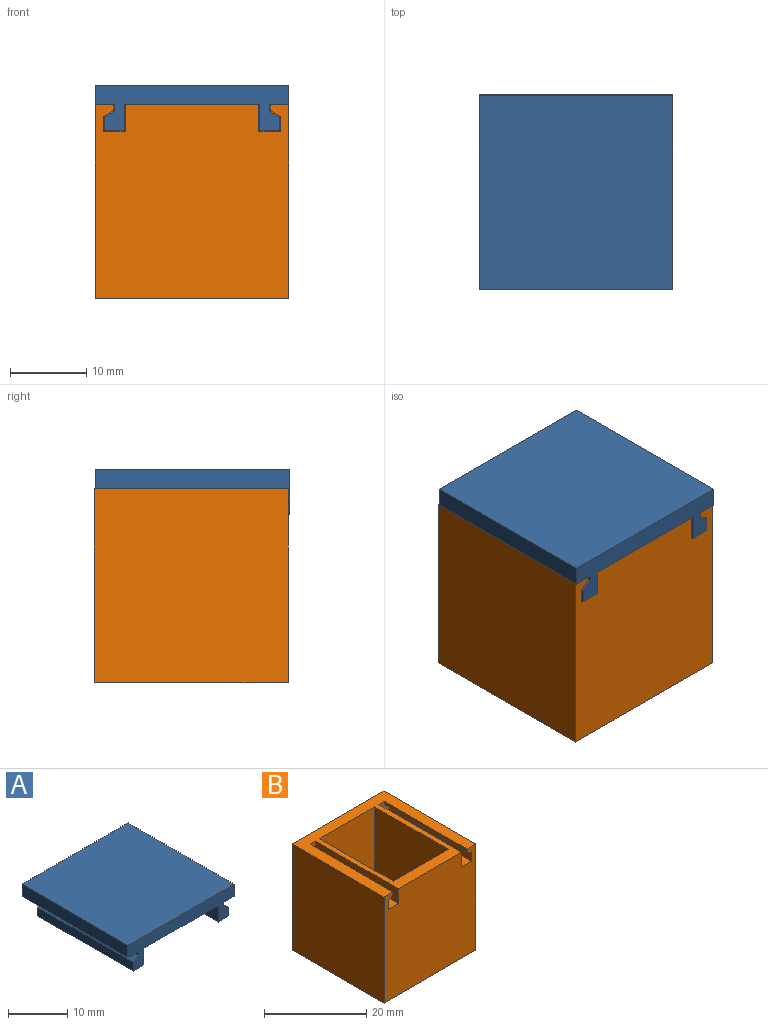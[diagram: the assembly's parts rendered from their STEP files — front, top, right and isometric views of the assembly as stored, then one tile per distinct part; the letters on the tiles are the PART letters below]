
ASSEMBLY  parts=2 mates=1
PART A: 18 faces, bbox 25.4x25.4x6 mm
  f0: plane 25.4x2.54mm, normal (0,1,0), area 64.5mm2, adj f1,f2,f4,f5
  f1: plane 25.4x2.54mm, normal (1,0,0), area 64.5mm2, adj f0,f3,f4,f5
  f2: plane 25.4x2.54mm, normal (-1,0,0), area 64.5mm2, adj f0,f3,f4,f5
  f3: plane 25.4x5.97mm, normal (0,-1,0), area 78.8mm2, adj f1,f2,f4,f5,f6,f7,f8,f9
  f4: plane 25.4x25.4mm, normal (0,0,-1), area 587.1mm2, adj f0,f1,f2,f3,f8,f9,f14,f15
  f5: plane 25.4x25.4mm, normal (0,0,1), area 645.2mm2, adj f0,f1,f2,f3
  f6: plane 22.86x1.78mm, normal (-1,0,0), area 40.6mm2, adj f3,f7,f10,f17
  f7: plane 22.86x2.54mm, normal (0,0,-1), area 58.1mm2, adj f3,f6,f8,f17
  f8: plane 22.86x3.43mm, normal (1,0,0), area 78.4mm2, adj f3,f4,f7,f17
  f9: plane 22.86x0.81mm, normal (-1,0,0), area 18.6mm2, adj f3,f4,f10,f17
  f10: plane 22.86x1.27mm, normal (-0.55,0,0.83), area 34.8mm2, adj f3,f6,f9,f17
  f11: plane 22.86x2.54mm, normal (0,0,-1), area 58.1mm2, adj f3,f12,f15,f16
  f12: plane 22.86x1.78mm, normal (1,0,0), area 40.6mm2, adj f3,f11,f13,f16
  f13: plane 22.86x1.27mm, normal (0.55,0,0.83), area 34.8mm2, adj f3,f12,f14,f16
  f14: plane 22.86x0.81mm, normal (1,0,0), area 18.6mm2, adj f3,f4,f13,f16
  f15: plane 22.86x3.43mm, normal (-1,0,0), area 78.4mm2, adj f3,f4,f11,f16
  f16: plane 3.43x2.54mm, normal (0,1,0), area 7.1mm2, adj f4,f11,f12,f13,f14,f15
  f17: plane 3.43x2.54mm, normal (0,1,0), area 7.1mm2, adj f4,f6,f7,f8,f9,f10
PART B: 23 faces, bbox 25.4x25.4x25.4 mm
  f0: plane 25.4x25.4mm, normal (0,1,0), area 645.2mm2, adj f2,f3,f4,f5
  f1: plane 25.4x25.4mm, normal (0,-1,0), area 628.3mm2, adj f2,f3,f4,f5,f11,f12,f13,f14
  f2: plane 25.4x25.4mm, normal (1,0,0), area 645.2mm2, adj f0,f1,f4,f5
  f3: plane 25.4x25.4mm, normal (-1,0,0), area 645.2mm2, adj f0,f1,f4,f5
  f4: plane 25.4x25.4mm, normal (0,0,-1), area 645.2mm2, adj f0,f1,f2,f3
  f5: plane 25.4x25.4mm, normal (0,0,1), area 266.4mm2, adj f0,f1,f2,f3,f6,f7,f8,f9
  f6: plane 22.86x20.29mm, normal (1,0,0), area 463.9mm2, adj f5,f7,f9,f10
  f7: plane 22.86x15.24mm, normal (0,1,0), area 348.4mm2, adj f5,f6,f8,f10
  f8: plane 22.86x20.29mm, normal (-1,0,0), area 463.9mm2, adj f5,f7,f9,f10
  f9: plane 22.86x15.24mm, normal (0,-1,0), area 348.4mm2, adj f5,f6,f8,f10
  f10: plane 20.29x15.24mm, normal (0,0,1), area 309.3mm2, adj f6,f7,f8,f9
  f11: plane 22.86x3.55mm, normal (1,0,0), area 81.1mm2, adj f1,f5,f12,f22
  f12: plane 22.86x2.79mm, normal (0,0,1), area 63.9mm2, adj f1,f11,f13,f22
  f13: plane 22.86x1.97mm, normal (-1,0,0), area 45.1mm2, adj f1,f12,f14,f22
  f14: plane 22.86x1.27mm, normal (-0.55,0,-0.84), area 34.8mm2, adj f1,f13,f15,f22
  f15: plane 22.86x0.74mm, normal (-1,0,0), area 16.9mm2, adj f1,f5,f14,f22
  f16: plane 22.86x1.97mm, normal (1,0,0), area 45.1mm2, adj f1,f17,f20,f21
  f17: plane 22.86x2.79mm, normal (0,0,1), area 63.9mm2, adj f1,f16,f18,f21
  f18: plane 22.86x3.55mm, normal (-1,0,0), area 81.1mm2, adj f1,f5,f17,f21
  f19: plane 22.86x0.74mm, normal (1,0,0), area 16.9mm2, adj f1,f5,f20,f21
  f20: plane 22.86x1.27mm, normal (0.55,0,-0.84), area 34.8mm2, adj f1,f16,f19,f21
  f21: plane 3.55x2.79mm, normal (0,-1,0), area 8.4mm2, adj f5,f16,f17,f18,f19,f20
  f22: plane 3.55x2.79mm, normal (0,-1,0), area 8.4mm2, adj f5,f11,f12,f13,f14,f15
PLACE A t=(3.99,-6.03,3.04)mm
PLACE B t=(3.99,-5.83,0.5)mm fixed
MATE slider A.f3 <-> B.f1  axis (0,-1,0) through (-8.71,-18.73,0.5)mm
